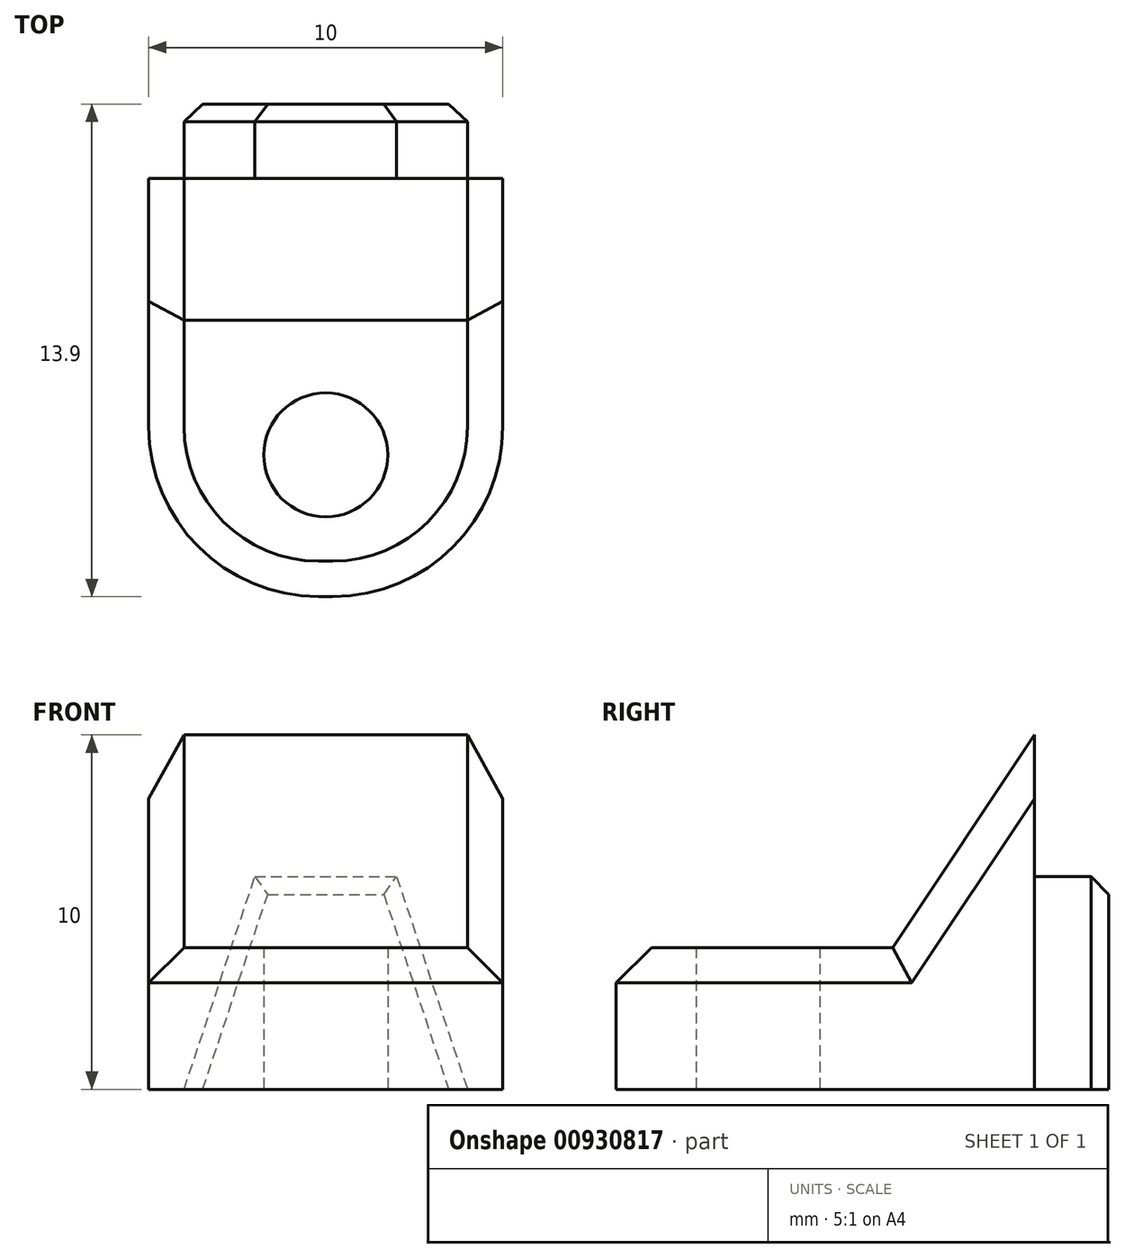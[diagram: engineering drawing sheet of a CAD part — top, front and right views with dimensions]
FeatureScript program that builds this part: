
annotation { "Feature Type Name" : "Feature", "Feature Type Description" : "" }
export const myFeature = defineFeature(function(context is Context, id is Id, definition is map)
    precondition{}
    {
        {
            var Q0;
            Q0=qCreatedBy(makeId("Right.planeOp"),FACE);
            var sketch = newSketch(context, id + "F0", { "sketchPlane" : qUnion([Q0])});
            skLineSegment(sketch, "E0", {"start": v(-11.8, 0) * mm, "end": v(-11.8, 4) * mm});
            skLineSegment(sketch, "E1", {"start": v(-11.8, 4) * mm, "end": v(-4, 4) * mm});
            skLineSegment(sketch, "E2", {"start": v(-4, 4) * mm, "end": v(0, 10) * mm});
            skLineSegment(sketch, "E3", {"start": v(0, 10) * mm, "end": v(0, 0) * mm});
            skLineSegment(sketch, "E4", {"start": v(0, 0) * mm, "end": v(-11.8, 0) * mm});
            skSolve(sketch);
        }
        {
            var Q0;
            Q0=qSketchRegion(id+"F0",true);
            extrude(context, id + "F1", {"entities" : qUnion([Q0]), "depth" : 10 * mm, "offsetDistance" : 25 * mm});
        }
        {
            var Q0;
            Q0=makeQuery(id+"F4Kgcb0rGnp8ghc_1.boolean.opBoolean","MERGE",FACE,{"derivedFrom":[makeQuery(id+"F1.opExtrude","SWEPT_FACE",FACE,{"disambiguationData":[OSD([sQuery(id+"F0.wireOp",EDGE,"E4")])]}),makeQuery(id+"F4Kgcb0rGnp8ghc_1.opExtrude","SWEPT_FACE",FACE,{"disambiguationData":[OSD([sQuery(id+"F88lFhElPqQXfID_1.wireOp",EDGE,"NgYCpmN1-ZXwI-vHYC-7Srw-qped2Mjlq2RP")])]})]});
            var sketch = newSketch(context, id + "F2", { "sketchPlane" : qUnion([Q0])});
            skLineSegment(sketch, "E5", {"start": v(5, 11.8) * mm, "end": v(5, 0) * mm, "construction": true});
            skCircle(sketch, "E6", {"center": v(5, 7.8) * mm, "radius": 1.75 * mm});
            skSolve(sketch);
        }
        {
            var Q0;
            Q0=qSketchRegion(id+"F2",true);
            var Q1;
            Q1=makeQuery(id+"F1.opExtrude","SWEPT_FACE",FACE,{"disambiguationData":[OSD([sQuery(id+"F0.wireOp",EDGE,"E1")])]});
            extrude(context, id + "F3", {"entities" : qUnion([Q0]), "operationType" : NewBodyOperationType.REMOVE, "endBound" : BoundingType.UP_TO_SURFACE, "oppositeDirection" : true, "depth" : 25 * mm, "endBoundEntityFace" : qUnion([Q1]), "offsetDistance" : 25 * mm});
        }
        {
            var Q0;
            Q0=makeQuery(id+"F1.opExtrude","SWEPT_FACE",FACE,{"disambiguationData":[OSD([sQuery(id+"F0.wireOp",EDGE,"E3")])]});
            var sketch = newSketch(context, id + "F4", { "sketchPlane" : qUnion([Q0])});
            skLineSegment(sketch, "E7", {"start": v(-9, 0) * mm, "end": v(-1, 0) * mm});
            skLineSegment(sketch, "E8", {"start": v(-1, 0) * mm, "end": v(-3, 6) * mm});
            skLineSegment(sketch, "E9", {"start": v(-3, 6) * mm, "end": v(-7, 6) * mm});
            skLineSegment(sketch, "E10", {"start": v(-7, 6) * mm, "end": v(-9, 0) * mm});
            skLineSegment(sketch, "E11", {"start": v(-5, 6) * mm, "end": v(-5, 0) * mm, "construction": true});
            skSolve(sketch);
        }
        {
            var Q0;
            Q0 = qSketchRegion(id + "F4", true);
            extrude(context, id + "F5", {"entities" : qUnion([Q0]), "operationType" : NewBodyOperationType.ADD, "depth" : 2.1 * mm, "offsetDistance" : 25 * mm});
        }
        {
            var Q0;
            Q0=makeQuery(id+"F1.opExtrude","CAP_EDGE",EDGE,{"disambiguationData":[OSD([sQuery(id+"F0.wireOp",EDGE,"E0")])],"isStart":true});
            var Q1;
            Q1=makeQuery(id+"F1.opExtrude","CAP_EDGE",EDGE,{"disambiguationData":[OSD([sQuery(id+"F0.wireOp",EDGE,"E0")])],"isStart":false});
            fillet(context, id + "F6", {"entities" : qUnion([Q0, Q1]), "radius" : 4.8 * mm, "tangentPropagation" : true, "allowEdgeOverflow" : false});
        }
        {
            var Q0;
            Q0=makeQuery(id+"F1.opExtrude","CAP_EDGE",EDGE,{"disambiguationData":[OSD([sQuery(id+"F0.wireOp",EDGE,"E1")])],"isStart":true});
            var Q1;
            Q1=makeQuery(id+"F1.opExtrude","CAP_EDGE",EDGE,{"disambiguationData":[OSD([sQuery(id+"F0.wireOp",EDGE,"E2")])],"isStart":true});
            var Q2;
            Q2=makeQuery(id+"F1.opExtrude","CAP_EDGE",EDGE,{"disambiguationData":[OSD([sQuery(id+"F0.wireOp",EDGE,"E2")])],"isStart":false});
            chamfer(context, id + "F7", {"entities" : qUnion([Q0, Q1, Q2]), "width" : 1 * mm, "tangentPropagation" : true});
        }
        {
            var Q0;
            Q0=makeQuery(id+"F5.opExtrude","CAP_EDGE",EDGE,{"disambiguationData":[OSD([sQuery(id+"F4.wireOp",EDGE,"E8")])],"isStart":false});
            var Q1;
            Q1=makeQuery(id+"F5.opExtrude","CAP_EDGE",EDGE,{"disambiguationData":[OSD([sQuery(id+"F4.wireOp",EDGE,"E9")])],"isStart":false});
            var Q2;
            Q2=makeQuery(id+"F5.opExtrude","CAP_EDGE",EDGE,{"disambiguationData":[OSD([sQuery(id+"F4.wireOp",EDGE,"E10")])],"isStart":false});
            chamfer(context, id + "F8", {"entities" : qUnion([Q0, Q1, Q2]), "width" : .5 * mm, "tangentPropagation" : true});
        }
    });
